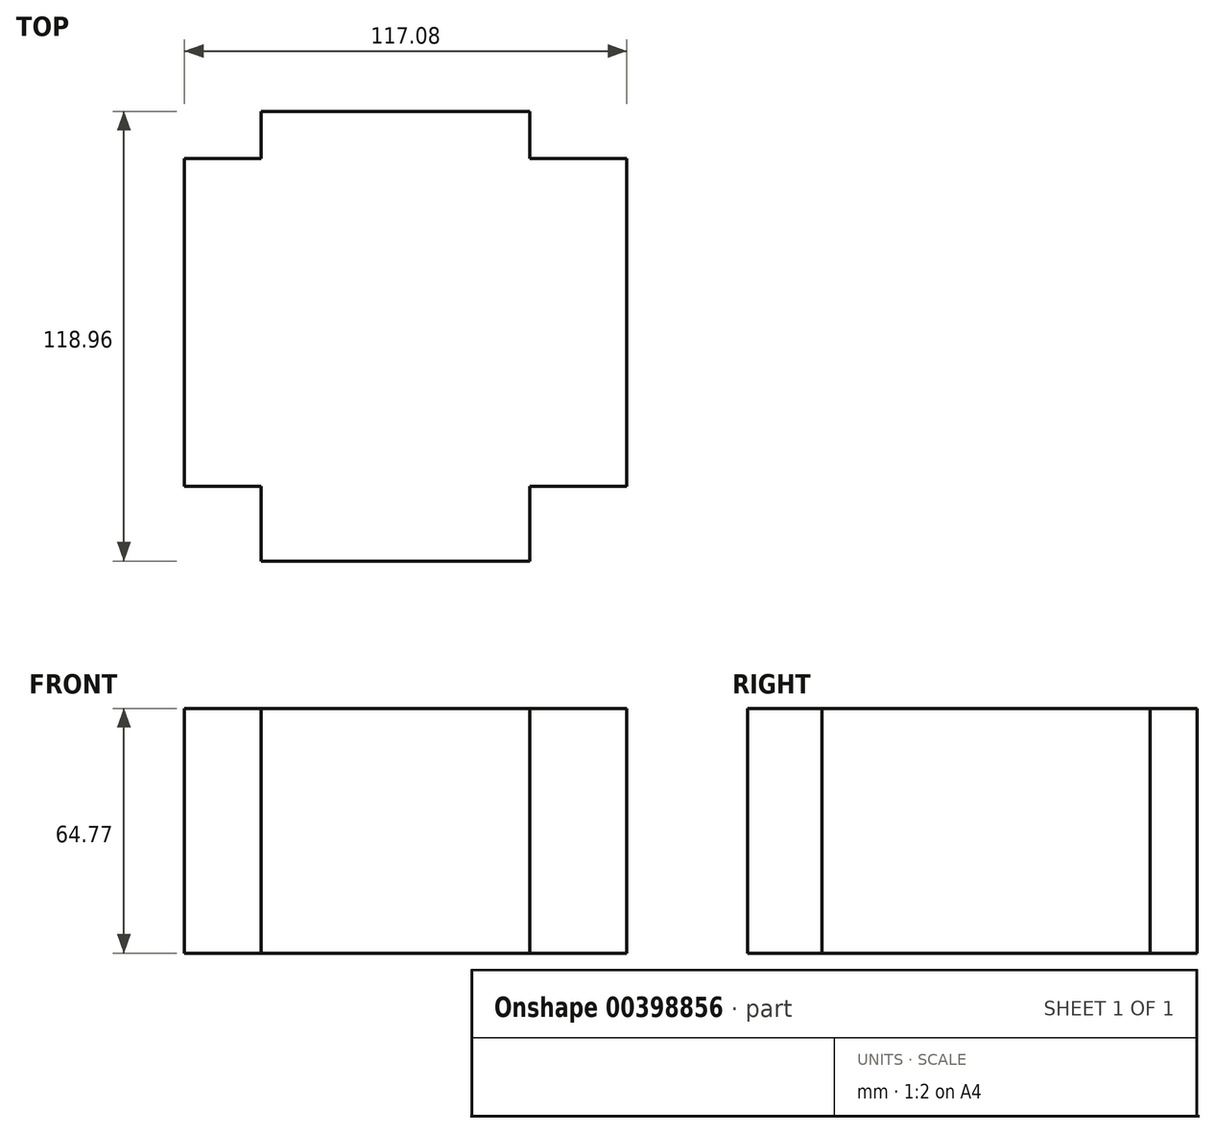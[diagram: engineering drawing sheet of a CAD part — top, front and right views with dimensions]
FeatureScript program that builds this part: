
annotation { "Feature Type Name" : "Feature", "Feature Type Description" : "" }
export const myFeature = defineFeature(function(context is Context, id is Id, definition is map)
    precondition{}
    {
        {
            var Q0;
            Q0=qCreatedBy(makeId("Top.planeOp"),FACE);
            var sketch = newSketch(context, id + "F0", { "sketchPlane" : qUnion([Q0])});
            skLineSegment(sketch, "E0.bottom", {"start": v(-35.25, 58.6) * mm, "end": v(35.9, 58.6) * mm});
            skLineSegment(sketch, "E0.top", {"start": v(-35.25, -60.35) * mm, "end": v(35.9, -60.35) * mm});
            skLineSegment(sketch, "E0.left", {"start": v(-35.25, 58.6) * mm, "end": v(-35.25, -60.35) * mm});
            skLineSegment(sketch, "E0.right", {"start": v(35.9, 58.6) * mm, "end": v(35.9, -60.35) * mm});
            skLineSegment(sketch, "E1.bottom", {"start": v(-55.56, 46.17) * mm, "end": v(61.52, 46.17) * mm});
            skLineSegment(sketch, "E1.top", {"start": v(-55.56, -40.62) * mm, "end": v(61.52, -40.62) * mm});
            skLineSegment(sketch, "E1.left", {"start": v(-55.56, 46.17) * mm, "end": v(-55.56, -40.62) * mm});
            skLineSegment(sketch, "E1.right", {"start": v(61.52, 46.17) * mm, "end": v(61.52, -40.62) * mm});
            skSolve(sketch);
        }
        {
            var Q0;
            Q0 = qSketchRegion(id + "F0", true);
            extrude(context, id + "F1", {"entities" : qUnion([Q0]), "depth" : 64.77 * mm});
        }
    });
